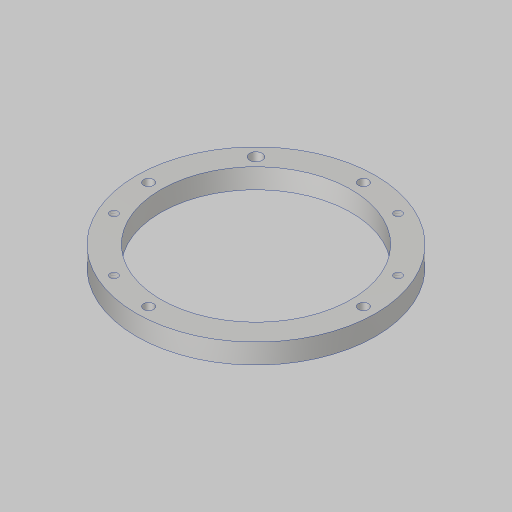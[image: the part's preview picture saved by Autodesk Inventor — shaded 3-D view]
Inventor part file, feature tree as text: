
AUTODESK INVENTOR PART (.ipt)
format: ipt  version: 2023.5 (Build 275446000, 446)  size: 166,400 bytes
history: native  units: in
note: dims shown in document units (in); Inventor stores cm internally (conversion verified against a paired STEP export)
features: sketch x4, hole x3, projected_geometry x2, extrude x1, pattern_circular x1
ambient origin geometry x8: Origin, YZ Plane, XZ Plane, XY Plane, X Axis, Y Axis, Z Axis, Center Point
bodies: Solid1 (feature_tree)
feature tree (11):
  extrude  "Extrusion1"  Depth=4.7244in
  hole  "Hole2"  [1 undecoded]
  pattern_circular  "Circular Pattern2"  Angle=45.0deg  [1 undecoded]
  hole  "Hole3"  [1 undecoded]
  hole  "Hole4"  [1 undecoded]
  sketch  "Sketch1"  dims[d0=2.7559in d1=4.7244in]
  sketch  "Sketch3"  dims[d2=0.3937in d3=0.0in]
  sketch  "Sketch4"  dims[d15=0.201in d16=0.75in d17=0.385in d18=0.25in d19=0.5635in d20=1.0in d21=0.8108in d22=1.5748in d23=360.0deg]
  sketch  "Sketch5"  dims[d25=1.5in d26=45.0deg d27=0.156in d28=0.38in d29=0.563in d30=0.12in d31=0.5635in d32=1.0in d33=0.8108in d34=45.0deg d35=0.249in d36=0.75in d37=0.563in d38=0.12in d39=0.5635in d40=1.0in d41=0.8108in d42=0.4803in d43=4.7244in d44=2.122in]
  projected_geometry  "Project Cut Edges2"
  projected_geometry  "Project Cut Edges3"
note: 4 required parameter values undecoded (feature->parameter linkage not recoverable at this tier; creation-order binding heuristic only, values carry confidence <= 0.55)
